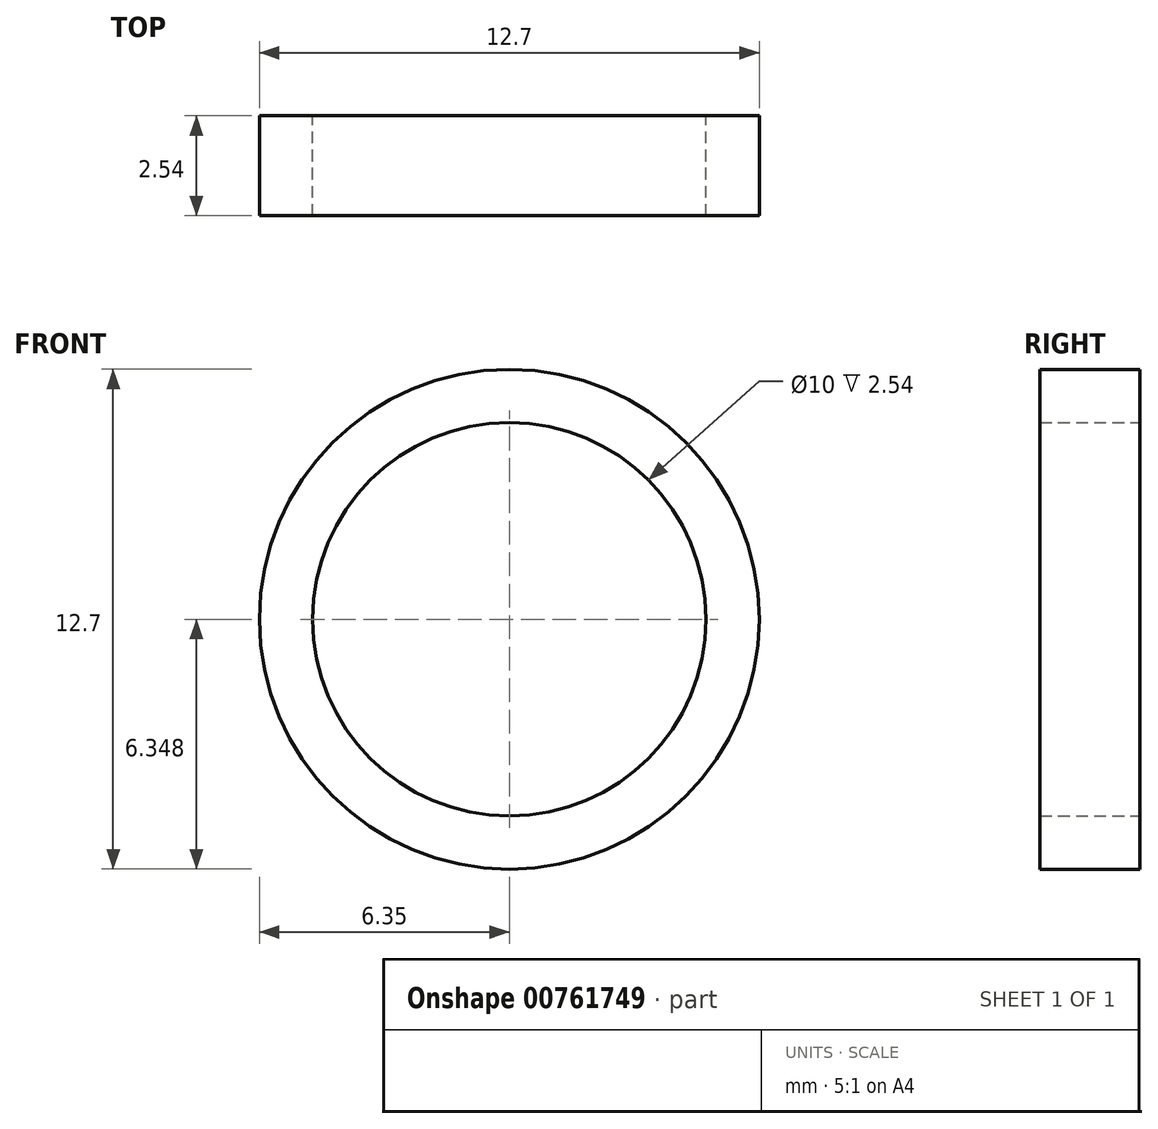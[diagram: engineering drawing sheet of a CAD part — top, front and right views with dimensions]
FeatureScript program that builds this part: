
annotation { "Feature Type Name" : "Feature", "Feature Type Description" : "" }
export const myFeature = defineFeature(function(context is Context, id is Id, definition is map)
    precondition{}
    {
        {
            var Q0;
            Q0=qCreatedBy(makeId("Front.planeOp"),FACE);
            var sketch = newSketch(context, id + "F0", { "sketchPlane" : qUnion([Q0])});
            skPoint(sketch, "E0.middle", {"position": v(0, -19.43) * mm});
            skPoint(sketch, "E1.visualSharp", {"position": v(-7.87, -15.53) * mm});
            skPoint(sketch, "E2.orphan", {"position": v(7.87, -15.53) * mm});
            skCircle(sketch, "E3", {"center": v(0, -9.06) * mm, "radius": 6.35 * mm});
            skCircle(sketch, "E4", {"center": v(0, -9.06) * mm, "radius": 5 * mm});
            skLineSegment(sketch, "E5", {"start": v(-4.43, -6.75) * mm, "end": v(0, -9.06) * mm});
            skLineSegment(sketch, "E6", {"start": v(0, -9.06) * mm, "end": v(4.43, -6.74) * mm});
            skLineSegment(sketch, "E7", {"start": v(0, -9.06) * mm, "end": v(0, -14.06) * mm});
            skPoint(sketch, "E0.top.start.orphan", {"position": v(7.87, -23.33) * mm});
            skPoint(sketch, "E8.start.orphan", {"position": v(-7.87, -23.33) * mm});
            skLineSegment(sketch, "E9", {"start": v(-4.43, -7.9) * mm, "end": v(0, -14.06) * mm});
            skPoint(sketch, "E9.startSnap0", {"position": v(-2.22, -7.9) * mm});
            skLineSegment(sketch, "E10", {"start": v(0, -14.06) * mm, "end": v(4.43, -6.74) * mm});
            skLineSegment(sketch, "E11", {"start": v(-4.43, -6.75) * mm, "end": v(4.43, -6.74) * mm});
            skLineSegment(sketch, "E12", {"start": v(0, -9.06) * mm, "end": v(-2.22, -7.9) * mm});
            skSolve(sketch);
        }
        {
            var Q0;
            Q0=makeQuery(id+"F0.imprint","IMPRINT",FACE,{"disambiguationData":[TD([[makeQuery(id+"F0.imprint","IMPRINT",EDGE,{"derivedFrom":sQuery(id+"F0.wireOp",EDGE,"E3")}),1.0]])]});
            var Q1;
            Q1=makeQuery(id+"F0.imprint","IMPRINT",FACE,{"disambiguationData":[TD([[makeQuery(id+"F0.imprint","IMPRINT",EDGE,{"derivedFrom":sQuery(id+"F0.wireOp",EDGE,"p85XBWY1-66Fp-Uzm2-WRaX-Vr9UEG9IWrfV")}),1.0]])]});
            var Q2;
            Q2=makeQuery(id+"F0.imprint","IMPRINT",FACE,{"disambiguationData":[TD([[makeQuery(id+"F0.imprint","IMPRINT",EDGE,{"derivedFrom":sQuery(id+"F0.wireOp",EDGE,"E0.top")}),-1.0]])]});
            extrude(context, id + "F1", {"entities" : qUnion([Q0, Q1, Q2]), "depth" : 2.54 * mm, "offsetDistance" : 25.4 * mm});
        }
    });
